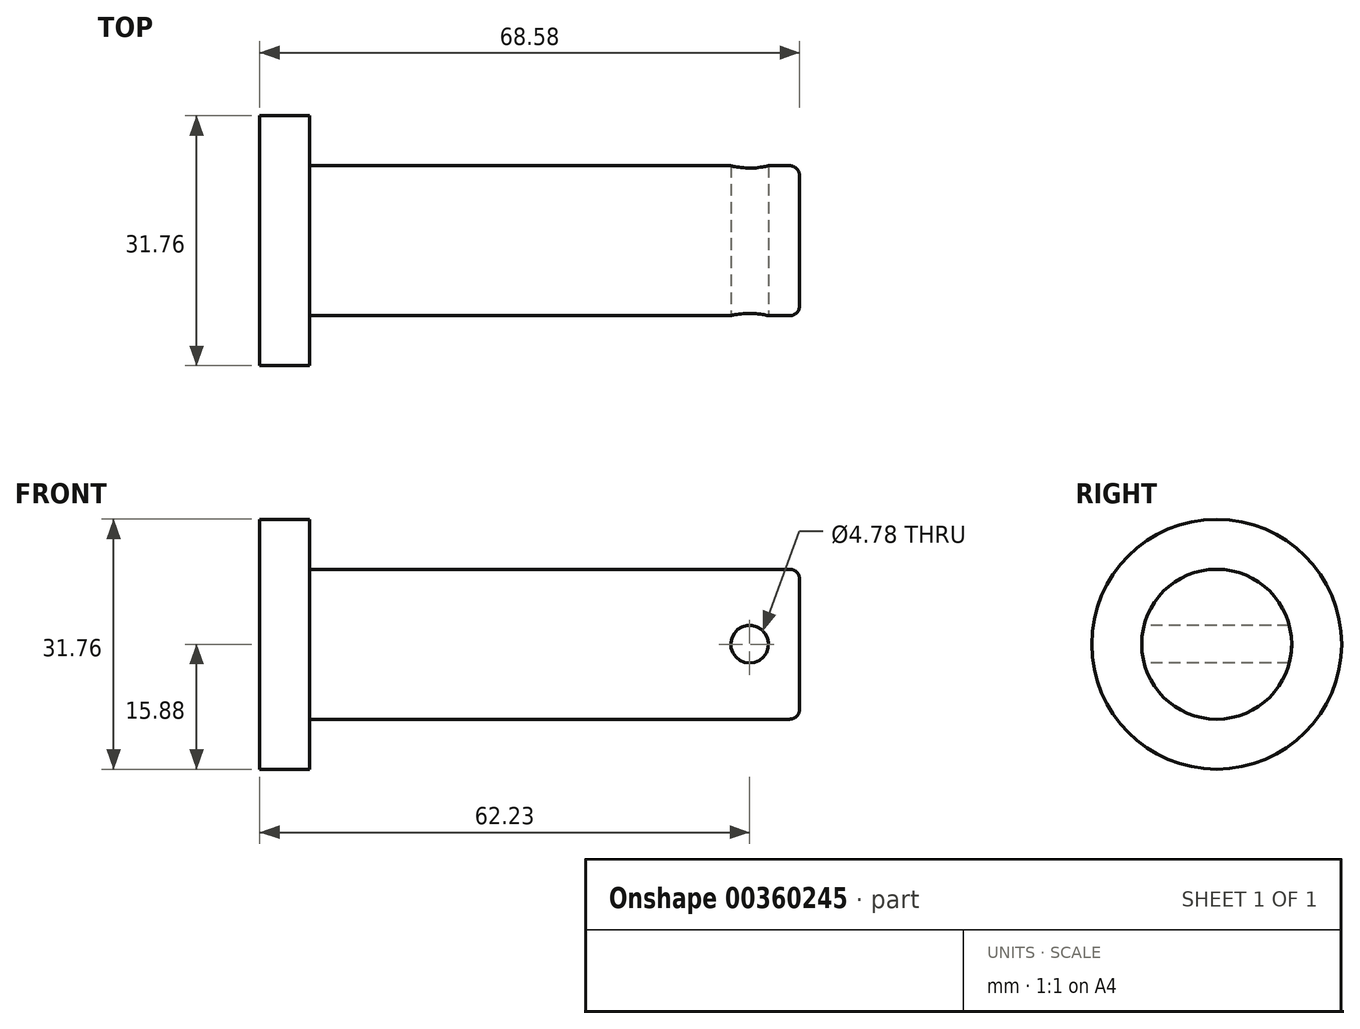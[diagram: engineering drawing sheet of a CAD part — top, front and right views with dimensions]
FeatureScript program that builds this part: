
annotation { "Feature Type Name" : "Feature", "Feature Type Description" : "" }
export const myFeature = defineFeature(function(context is Context, id is Id, definition is map)
    precondition{}
    {
        {
            var Q0;
            Q0=qCreatedBy(makeId("Right.planeOp"),FACE);
            var sketch = newSketch(context, id + "F0", { "sketchPlane" : qUnion([Q0])});
            skCircle(sketch, "E0", {"center": v(0, 0) * mm, "radius": 15.88 * mm});
            skSolve(sketch);
        }
        {
            var Q0;
            Q0=makeQuery(id+"F0.imprint","IMPRINT",FACE,{"disambiguationData":[TD([[makeQuery(id+"F0.imprint","IMPRINT",EDGE,{"derivedFrom":sQuery(id+"F0.wireOp",EDGE,"E0")}),1.0]])]});
            extrude(context, id + "F1", {"entities" : qUnion([Q0]), "depth" : 6.35 * mm});
        }
        {
            var Q0;
            Q0=makeQuery(id+"F1.opExtrude","CAP_FACE",FACE,{"disambiguationData":[OSD([sQuery(id+"F0.wireOp",EDGE,"E0")])],"isStart":false});
            var sketch = newSketch(context, id + "F2", { "sketchPlane" : qUnion([Q0])});
            skCircle(sketch, "E1", {"center": v(0, 0) * mm, "radius": 9.53 * mm});
            skSolve(sketch);
        }
        {
            var Q0;
            Q0=makeQuery(id+"F2.imprint","IMPRINT",FACE,{"disambiguationData":[TD([[makeQuery(id+"F2.imprint","IMPRINT",EDGE,{"derivedFrom":sQuery(id+"F2.wireOp",EDGE,"E1")}),1.0]])]});
            extrude(context, id + "F3", {"entities" : qUnion([Q0]), "operationType" : NewBodyOperationType.ADD, "depth" : 62.23 * mm});
        }
        {
            var Q0;
            Q0=qCreatedBy(makeId("Front.planeOp"),FACE);
            var sketch = newSketch(context, id + "F4", { "sketchPlane" : qUnion([Q0])});
            skLineSegment(sketch, "E2", {"start": v(1.1, 0) * mm, "end": v(68.58, 0) * mm, "construction": true});
            skCircle(sketch, "E3", {"center": v(62.23, 0) * mm, "radius": 2.39 * mm});
            skSolve(sketch);
        }
        {
            var Q0;
            Q0=makeQuery(id+"F4.imprint","IMPRINT",FACE,{"disambiguationData":[TD([[makeQuery(id+"F4.imprint","IMPRINT",EDGE,{"derivedFrom":sQuery(id+"F4.wireOp",EDGE,"E3")}),1.0]])]});
            var Q1;
            Q1=sQuery(id+"F4.wireOp",EDGE,"E3");
            extrude(context, id + "F5", {"entities" : qUnion([Q0]), "operationType" : NewBodyOperationType.REMOVE, "surfaceEntities" : qUnion([Q1]), "oppositeDirection" : true, "depth" : 25.4 * mm, "hasSecondDirection" : true, "secondDirectionOppositeDirection" : false, "secondDirectionDepth" : 25.4 * mm});
        }
        {
            var Q0;
            Q0=makeQuery(id+"F3.opExtrude","CAP_FACE",FACE,{"disambiguationData":[OSD([sQuery(id+"F2.wireOp",EDGE,"E1")])],"isStart":false});
            fillet(context, id + "F6", {"entities" : qUnion([Q0]), "radius" : 1.27 * mm, "tangentPropagation" : true, "allowEdgeOverflow" : false});
        }
    });
